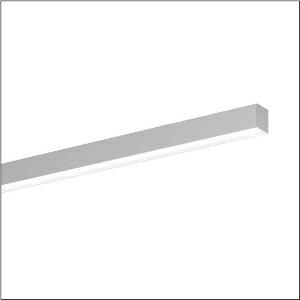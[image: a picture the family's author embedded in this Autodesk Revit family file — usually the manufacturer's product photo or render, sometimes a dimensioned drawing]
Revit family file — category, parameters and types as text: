
# Revit family: silica_r__21_51mx23db45sb_b235
name_source: partatom
category: Lighting Fixtures
units: mm (PartAtom-declared; Revit-internal decimal feet)

## family parameters
Cut with Voids When Loaded = No
Host = Face
Light Source = No
Part Type = Normal
Room Calculation Point = No
Round Connector Dimension = Use Diameter
Shared = No

## types (1)
- --- (1 x LED, 4100 lm, 28.1 W, 4000K)
    Apparent Load = 28 VA
    CIE Flux Codes = 78 96 99 100 100
    Color Rendering = 80
    Color Temperature = 4000K
    Default Elevation = 1800 mm
    Description = Silica® 21, office luminaire, primary optical cover: prismatic diffuser, of PMMA, CAT 2 (L<= 3000cd/m²), light emission: direct distribution, primary light characteristic: symmetric, installation type: surface-mounted, LED, rated luminous flux: 4.100lm, luminous efficacy: 146lm/W, light colour: 840, colour temperature: 4000K, with terminal, 3+2-pole, max. 2.5mm², mains connection: 220..240V, AC, 50/60Hz, rated input power: 28.1W, luminaire housing, of aluminium, metallic grey (RAL 9006), length: 1.504mm, width: 53mm, height: 53mm, protection rating (complete): IP20, insulation class (complete): insulation class I (protective earthing), certification: CE, permissible operating ambient temperature: 0..+35°C, standard: EN 50419, packaging unit: 1 piece
    Height = 0 mm  [stored 0 ft]
    Lamp = 1 x LED
    Lamp Light Flux = 4100 lm
    Lamp Power = 28.1 W
    Lamp count = 1
    Length = 1504 mm
    Luminous efficacy = 146 lm/W
    Manufacturer = Siteco
    ModVariant = No
    Model = 51MX23DB45SB
    Mounting Place = Ceiling
    Mounting Type = Recessed
    Number of Poles = 1
    OnlyDefault = Yes
    Power Factor = 1
    Product Name = Silica® 21
    Product group = office luminaire | ceiling recessed
    ProductGroupID = 401
    Protection Class = Protection class I
    Protection Degree = IP 20
    RLX_Detail_Level = 1
    RLX_Emergency_Light_Flux = 0 lm
    RLX_Emergency_Type = 0
    RLX_Emergency_Type_DB = No
    RlxData = <blob elided: 21365 chars, md5=4e780426>
    Socket = socket
    Standby Power = 0 W
    System Light Flux = 4100 lm
    System Power = 28 W
    Type Comments = factory setting: luminous flux: 100 % | dim-lin: 254 | 323 mA
    Type Image = l_1297768.jpg
    URL = http://relux.com
    VarID = @adj_049697
    Voltage = 0 V
    Weight = 0.00 kg
    Width = 53 mm

note: [stored X ft] marks values corroborated as IEEE doubles in the binary element streams (Revit-internal decimal feet)

## geometry (parser evidence)
native form markers: Blend x4, Sweep x10
no freeform markers — native parametric forms only
